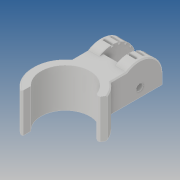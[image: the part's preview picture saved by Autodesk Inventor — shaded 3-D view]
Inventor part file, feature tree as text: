
AUTODESK INVENTOR PART (.ipt)
format: ipt  version: 2019 (Build 230136000, 136)  size: 329,728 bytes
history: native  units: mm
features: extrude x7, sketch x7, other x4, hole x1, chamfer x1, pattern_circular x1
ambient origin geometry x8: Origin, YZ Plane, XZ Plane, XY Plane, X Axis, Y Axis, Z Axis, Center Point
bodies: Solide1 (feature_tree)
feature tree (21):
  other  "viseur_base.ipt"
  extrude  "Extrusion1"  Depth=10.0mm
  hole  "Perçage3"  [1 undecoded]
  extrude  "Extrusion6"  Depth=40.0mm
  other  "Plan de construction14"
  sketch  "Esquisse17"
  extrude  "Extrusion8"  Depth=10.0mm TaperAngle=0.0deg
  extrude  "Extrusion9"  Depth=0.5mm
  extrude  "Extrusion10"  Depth=8.0mm
  extrude  "Extrusion11"  Depth=19.0mm
  chamfer  "Chanfrein4"  Distance=12.0mm
  extrude  "Extrusion12"  Depth=4.0mm TaperAngle=0.0deg
  pattern_circular  "Réseau circulaire1"  [2 undecoded]
  other  "Solide1::viseur_base.ipt"
  other  "FonctionRepérage1"
  sketch  "Esquisse1"
  sketch  "Esquisse12"
  sketch  "Esquisse13"
  sketch  "Esquisse14"
  sketch  "Esquisse18"
  sketch  "Esquisse19"
note: 3 required parameter values undecoded (feature->parameter linkage not recoverable at this tier; creation-order binding heuristic only, values carry confidence <= 0.55)
